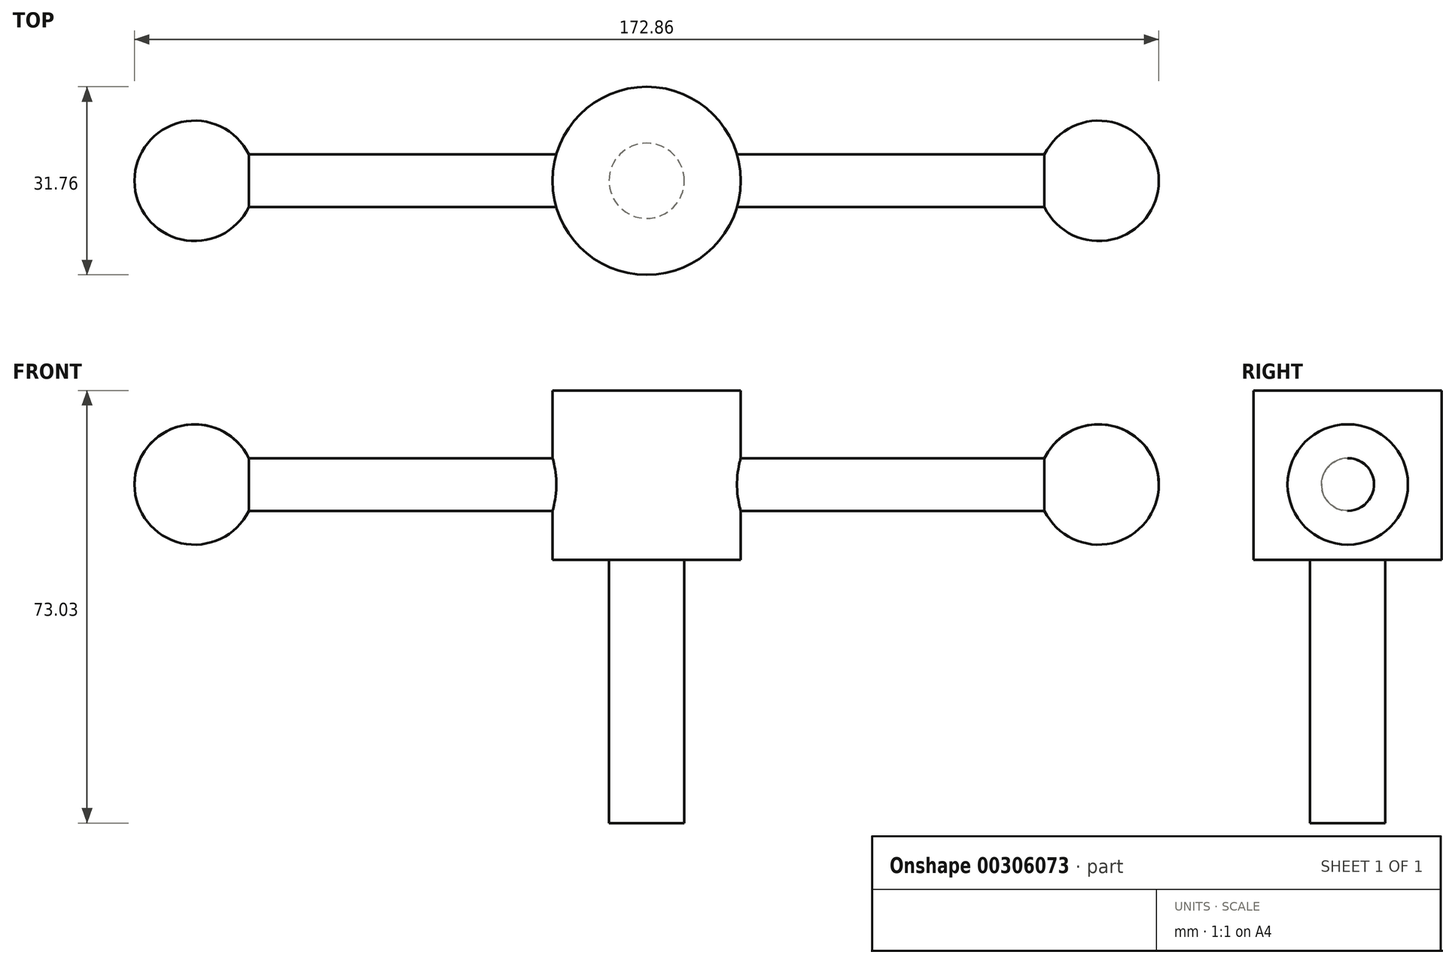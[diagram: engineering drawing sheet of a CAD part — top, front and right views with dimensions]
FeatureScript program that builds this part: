
annotation { "Feature Type Name" : "Feature", "Feature Type Description" : "" }
export const myFeature = defineFeature(function(context is Context, id is Id, definition is map)
    precondition{}
    {
        {
            var Q0;
            Q0=qCreatedBy(makeId("Top.planeOp"),FACE);
            var sketch = newSketch(context, id + "F0", { "sketchPlane" : qUnion([Q0])});
            skCircle(sketch, "E0", {"center": v(0, 0) * mm, "radius": 15.87 * mm});
            skSolve(sketch);
        }
        {
            var Q0;
            Q0 = qSketchRegion(id + "F0", true);
            extrude(context, id + "F1", {"entities" : qUnion([Q0]), "depth" : 28.57 * mm});
        }
        {
            var Q0;
            Q0=makeQuery(id+"F1.opExtrude","CAP_FACE",FACE,{"disambiguationData":[OSD([sQuery(id+"F0.wireOp",EDGE,"E0")])],"isStart":true});
            var sketch = newSketch(context, id + "F2", { "sketchPlane" : qUnion([Q0])});
            skCircle(sketch, "E1", {"center": v(0, 0) * mm, "radius": 6.35 * mm});
            skSolve(sketch);
        }
        {
            var Q0;
            Q0 = qSketchRegion(id + "F2", true);
            extrude(context, id + "F3", {"entities" : qUnion([Q0]), "operationType" : NewBodyOperationType.ADD, "depth" : 44.45 * mm});
        }
        {
            var Q0;
            Q0=qCreatedBy(makeId("Right.planeOp"),FACE);
            var sketch = newSketch(context, id + "F4", { "sketchPlane" : qUnion([Q0])});
            skCircle(sketch, "E2", {"center": v(0, 12.7) * mm, "radius": 4.45 * mm});
            skSolve(sketch);
        }
        {
            var Q0;
            Q0 = qSketchRegion(id + "F4", true);
            extrude(context, id + "F5", {"entities" : qUnion([Q0]), "operationType" : NewBodyOperationType.ADD, "endBound" : BoundingType.SYMMETRIC, "depth" : 152.4 * mm});
        }
        {
            var Q0;
            Q0=qCreatedBy(makeId("Front.planeOp"),FACE);
            var sketch = newSketch(context, id + "F6", { "sketchPlane" : qUnion([Q0])});
            skLineSegment(sketch, "E3", {"start": v(-76.27, 12.7) * mm, "end": v(-57.35, 12.7) * mm, "construction": true});
            skArc(sketch, "E4", {"start": v(-66.11, 12.7) * mm, "mid": v(-76.27, 22.86) * mm, "end": v(-86.43, 12.7) * mm});
            skLineSegment(sketch, "E5", {"start": v(-66.11, 12.7) * mm, "end": v(-86.43, 12.7) * mm});
            skLineSegment(sketch, "E6", {"start": v(0, 59.56) * mm, "end": v(0, -56.85) * mm, "construction": true});
            skArc(sketch, "E7.MirrorCS", {"start": v(66.11, 12.7) * mm, "mid": v(76.27, 22.86) * mm, "end": v(86.43, 12.7) * mm});
            skLineSegment(sketch, "E8.MirrorCS", {"start": v(76.27, 12.7) * mm, "end": v(57.35, 12.7) * mm, "construction": true});
            skLineSegment(sketch, "E9.MirrorCS", {"start": v(66.11, 12.7) * mm, "end": v(86.43, 12.7) * mm});
            skSolve(sketch);
        }
        {
            var Q0;
            Q0 = qSketchRegion(id + "F6", true);
            var Q1;
            Q1=sQuery(id+"F6.wireOp",EDGE,"E3");
            revolve(context, id + "F7", {"operationType" : NewBodyOperationType.ADD, "entities" : qUnion([Q0]), "axis" : qUnion([Q1]), "revolveType" : RevolveType.FULL});
        }
    });
